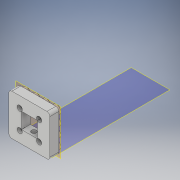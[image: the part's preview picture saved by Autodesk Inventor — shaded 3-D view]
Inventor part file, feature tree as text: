
AUTODESK INVENTOR PART (.ipt)
format: ipt  version: 2019.3 (Build 233278000, 278)  size: 297,984 bytes
history: native  units: mm
features: sketch x8, extrude x5, reference x4, plane x2, other x2, sweep x1
ambient origin geometry x8: Origin, YZ Plane, XZ Plane, XY Plane, X Axis, Y Axis, Z Axis, Center Point
bodies: Solid1 (feature_tree)
feature tree (22):
  extrude  "Extrusion1"  Depth=15.0mm TaperAngle=0.0deg
  plane  "Work Plane1"
  extrude  "Extrusion2"  Depth=1.0mm
  sketch  "Sketch3"  dims[d6=1.0mm d7=1.0mm]
  sketch  "Sketch4"  dims[d9=2.0mm d10=6.0mm]
  plane  "Work Plane2"
  sweep  "Sweep1"
  extrude  "Extrusion3"  Depth=6.0mm
  extrude  "Extrusion4"  Depth=4.0mm
  extrude  "Extrusion5"  TaperAngle=135.0deg  [1 undecoded]
  sketch  "Sketch1"  dims[d0=5.0mm d1=0.0mm d2=15.0mm d3=0.0mm]
  reference  "Reference1"
  sketch  "Sketch2"  dims[d4=1.0mm d5=1.0mm]
  reference  "Reference2"
  reference  "Reference3"
  reference  "Reference4"
  sketch  "Sketch5"  dims[d11=6.0mm d12=4.0mm]
  sketch  "Sketch6"  dims[d13=40.0mm d15=17.0mm d16=40.0mm d18=17.0mm d21=135.0deg]
  sketch  "Sketch7"  dims[d23=5.0mm]
  sketch  "Sketch8"  dims[d24=0.0mm d25=0.0mm d26=7.5mm d27=13.5mm d28=34.5mm d29=12.0mm d30=0.0mm d31=8.0mm d32=12.0mm d33=0.0mm d34=1.1mm d35=1.1mm d36=1.1mm d37=1.1mm d38=5.2mm d39=0.0mm d40=0.75mm d41=0.75mm d42=0.75mm d43=0.75mm d44=0.75mm d45=0.75mm d46=0.75mm d47=0.75mm d48=0.75mm d49=0.75mm d50=0.75mm d51=0.75mm]
  other  "Assembly1"
  other  "WeightHolder:1"
note: 1 required parameter value undecoded (feature->parameter linkage not recoverable at this tier; creation-order binding heuristic only, values carry confidence <= 0.55)
